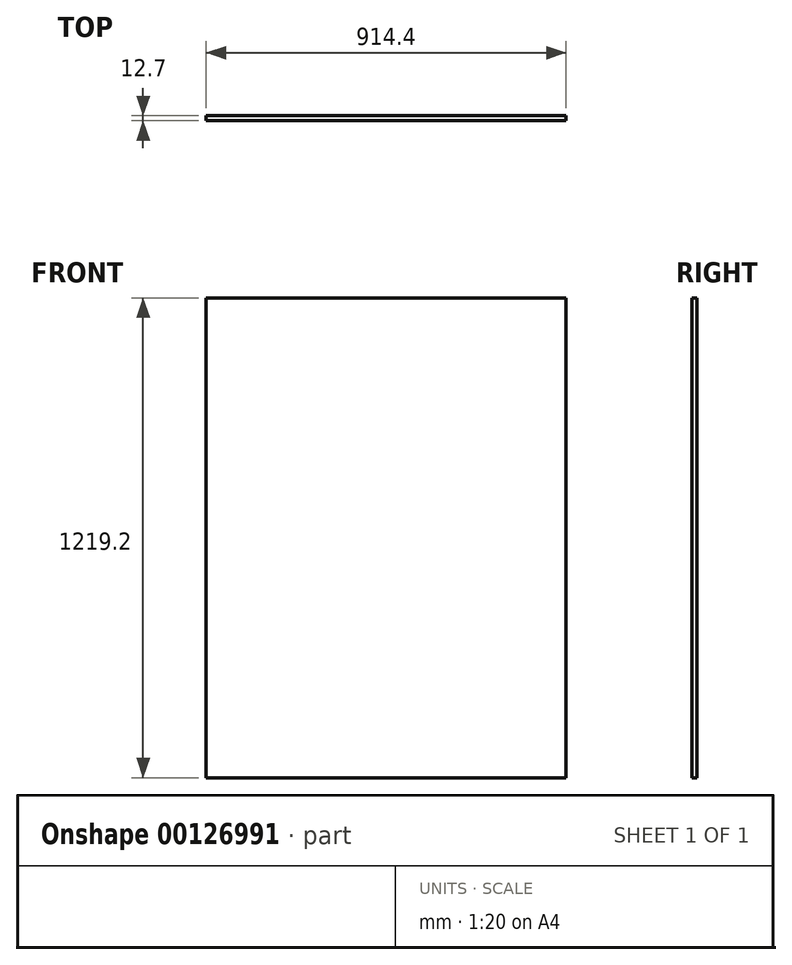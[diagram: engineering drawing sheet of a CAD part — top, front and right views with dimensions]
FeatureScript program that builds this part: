
annotation { "Feature Type Name" : "Feature", "Feature Type Description" : "" }
export const myFeature = defineFeature(function(context is Context, id is Id, definition is map)
    precondition{}
    {
        {
            var Q0;
            Q0=qCreatedBy(makeId("Front.planeOp"),FACE);
            var sketch = newSketch(context, id + "F0", { "sketchPlane" : qUnion([Q0])});
            skLineSegment(sketch, "E0.bottom", {"start": v(0, -1219.2) * mm, "end": v(914.4, -1219.2) * mm});
            skLineSegment(sketch, "E0.top", {"start": v(0, 0) * mm, "end": v(914.4, 0) * mm});
            skLineSegment(sketch, "E0.left", {"start": v(0, 0) * mm, "end": v(0, -1219.2) * mm});
            skLineSegment(sketch, "E0.right", {"start": v(914.4, 0) * mm, "end": v(914.4, -1219.2) * mm});
            skSolve(sketch);
        }
        {
            var Q0;
            Q0 = qSketchRegion(id + "F0", true);
            extrude(context, id + "F1", {"entities" : qUnion([Q0]), "depth" : 12.7 * mm});
        }
    });
